# Revit family: A307 Bolts-Side
name_source: partatom
category: Detail Items
revit_build: Autodesk Revit Architecture 2012 (Build: 20110210_1515)
units: mm (PartAtom-declared; Revit-internal decimal feet)

## types (9) — shared parameters

## per-type parameters (varying)
| type | Diameter | F3 | F4 | H diff | H1 | Head Height | Keynote | Washer Height |
| 1/2" | 0.50" | 0.24" | 0.47" | 0.06" | 0.25" | 0.31" | 05 05 23.A1 | 0.03" |
| 5/8" | 0.63" | 0.29" | 0.59" | 0.08" | 0.31" | 0.39" | 05 05 23.A2 | 0.04" |
| 3/4" | 0.75" | 0.35" | 0.70" | 0.10" | 0.38" | 0.48" | 05 05 23.A3 | 0.05" |
| 7/8" | 0.88" | 0.41" | 0.82" | 0.11" | 0.44" | 0.55" | 05 05 23.A4 | 0.06" |
| 1" | 1.00" | 0.47" | 0.94" | 0.13" | 0.50" | 0.63" | 05 05 23.A5 | 0.06" |
| 1 1/4" | 1.25" | 0.59" | 1.17" | 0.15" | 0.63" | 0.78" | 05 05 23.A7 | 0.08" |
| 1 1/8" | 1.13" | 0.53" | 1.06" | 0.14" | 0.56" | 0.70" | 05 05 23.A6 | 0.07" |
| 1 3/8" | 1.38" | 0.65" | 1.29" | 0.17" | 0.69" | 0.86" | 05 05 23.A8 | 0.09" |
| 1 1/2" | 1.50" | 0.70" | 1.41" | 0.19" | 0.75" | 0.94" | 05 05 23.A9 | 0.09" |

## geometry (parser evidence)
native form markers: Sweep x1
no freeform markers — native parametric forms only
